# Revit family: Skylight_Fakro_FX
name_source: partatom
category: Generic Models
units: mm (PartAtom-declared; Revit-internal decimal feet)

## family parameters
Always vertical = No
Can host rebar = No
Classification Number = 23.30.30.14
Cut with Voids When Loaded = No
Host = Roof
Maintain Annotation Orientation = No
Part Type = Normal
Room Calculation Point = No
Round Connector Dimension = Use Diameter
Shared = No

## types (11) — shared parameters
Assembly Code = B3020110
Keynote = 08 62 00
Manufacturer = Fakro USA
Manufacturer Fax = 630-543-1011
Manufacturer Website = http://www.fakrousa.com
Model = FX
Product Data = http://www.fakrousa.com
Revision = R1_2016-01
Sales Information = http://www.fakrousa.com
URL = http://www.fakrousa.com
zero-valued in all types: Cost, Default Elevation, Expected Lifespan (Years), Maintenance Schedule (Months), Warranty Duration (Years)

## per-type parameters (varying)
| type | Description | Kaptur width | Side Length | Unit Height | Unit Width |
| 48x46 | Fakro FX Skylight - 48x46 | 1236 mm  [stored 4.05512 ft] | 1180 mm  [stored 3.87139 ft] | 1178 mm | 1232 mm  [stored 4.04199 ft] |
| 48x27 | Fakro FX Skylight - 48x27 | 1236 mm  [stored 4.05512 ft] | 701 mm  [stored 2.29987 ft] | 699 mm  [stored 2.29331 ft] | 1232 mm  [stored 4.04199 ft] |
| 32x55 | Fakro FX Skylight - 32x55 | 830 mm  [stored 2.7231 ft] | 1399 mm  [stored 4.5899 ft] | 1397 mm  [stored 4.58333 ft] | 826 mm  [stored 2.70997 ft] |
| 32x46 | Fakro FX Skylight - 32x46 | 830 mm  [stored 2.7231 ft] | 1180 mm  [stored 3.87139 ft] | 1178 mm | 826 mm  [stored 2.70997 ft] |
| 32x38 | Fakro FX Skylight - 32x38 | 830 mm  [stored 2.7231 ft] | 980 mm  [stored 3.21522 ft] | 978 mm  [stored 3.20866 ft] | 826 mm  [stored 2.70997 ft] |
| 24x70 | Fakro FX Skylight - 24x70 | 627 mm  [stored 2.05709 ft] | 1799 mm  [stored 5.90223 ft] | 1797 mm  [stored 5.89567 ft] | 623 mm  [stored 2.04396 ft] |
| 24x55 | Fakro FX Skylight - 24x55 | 627 mm  [stored 2.05709 ft] | 1399 mm  [stored 4.5899 ft] | 1397 mm  [stored 4.58333 ft] | 623 mm  [stored 2.04396 ft] |
| 24x46 | Fakro FX Skylight - 24x46 | 627 mm  [stored 2.05709 ft] | 1180 mm  [stored 3.87139 ft] | 1178 mm | 623 mm  [stored 2.04396 ft] |
| 24x38 | Fakro FX Skylight - 24x38 | 627 mm  [stored 2.05709 ft] | 980 mm  [stored 3.21522 ft] | 978 mm  [stored 3.20866 ft] | 623 mm  [stored 2.04396 ft] |
| 24x27 | Fakro FX Skylight - 24x27 | 627 mm  [stored 2.05709 ft] | 701 mm  [stored 2.29987 ft] | 699 mm  [stored 2.29331 ft] | 623 mm  [stored 2.04396 ft] |
| 16x46 | Fakro FX Skylight - 16x46 | 423 mm  [stored 1.3878 ft] | 1180 mm  [stored 3.87139 ft] | 1178 mm | 419 mm |

note: [stored X ft] marks values corroborated as IEEE doubles in the binary element streams (Revit-internal decimal feet)

## geometry (parser evidence)
native form markers: Blend x4
no freeform markers — native parametric forms only
